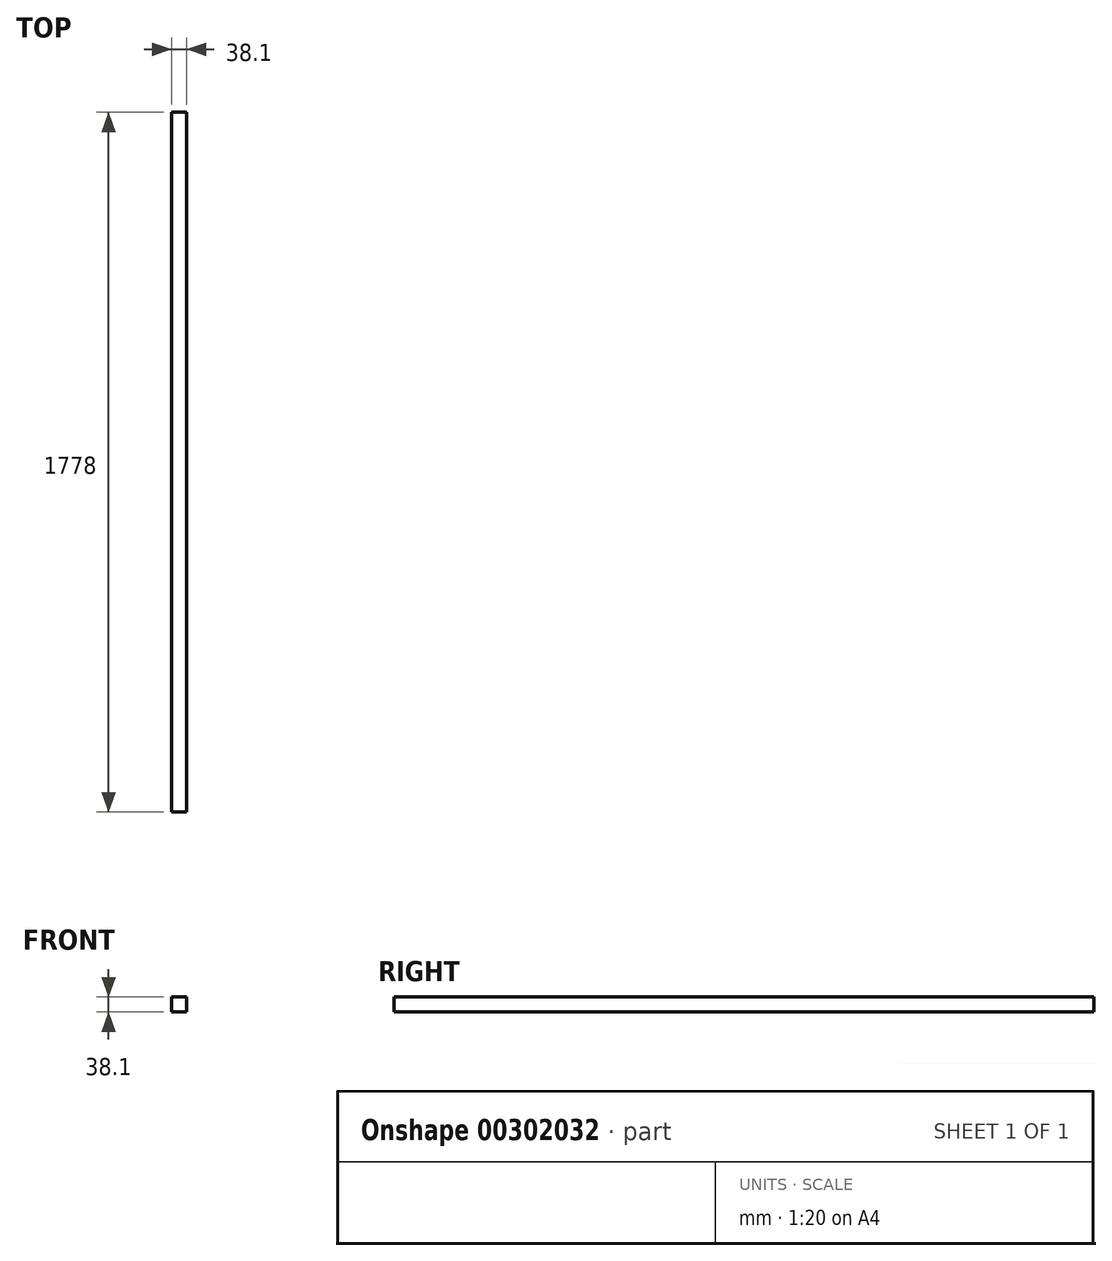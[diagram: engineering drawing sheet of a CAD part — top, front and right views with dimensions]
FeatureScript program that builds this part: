
annotation { "Feature Type Name" : "Feature", "Feature Type Description" : "" }
export const myFeature = defineFeature(function(context is Context, id is Id, definition is map)
    precondition{}
    {
        {
            var Q0;
            Q0=qCreatedBy(makeId("Front.planeOp"),FACE);
            var sketch = newSketch(context, id + "F0", { "sketchPlane" : qUnion([Q0])});
            skLineSegment(sketch, "E0.bottom", {"start": v(0, 0) * mm, "end": v(38.1, 0) * mm});
            skLineSegment(sketch, "E0.top", {"start": v(0, 38.1) * mm, "end": v(38.1, 38.1) * mm});
            skLineSegment(sketch, "E0.left", {"start": v(0, 0) * mm, "end": v(0, 38.1) * mm});
            skLineSegment(sketch, "E0.right", {"start": v(38.1, 0) * mm, "end": v(38.1, 38.1) * mm});
            skSolve(sketch);
        }
        {
            var Q0;
            Q0 = qSketchRegion(id + "F0", true);
            extrude(context, id + "F1", {"entities" : qUnion([Q0]), "depth" : 1778 * mm});
        }
    });
